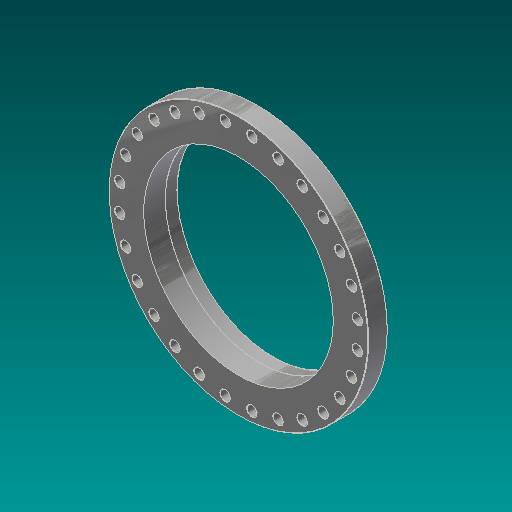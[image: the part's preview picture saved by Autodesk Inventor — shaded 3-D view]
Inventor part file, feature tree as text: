
AUTODESK INVENTOR PART (.ipt)
format: ipt  version: 2017.3 (Build 213257000, 257)  size: 361,472 bytes
history: native  units: in
note: dims shown in document units (in); Inventor stores cm internally (conversion verified against a paired STEP export)
features: sketch x7, extrude x5, chamfer x3, fillet x2, hole x1, pattern_circular x1, revolve x1, projected_geometry x1
ambient origin geometry x8: Origin, YZ Plane, XZ Plane, XY Plane, X Axis, Y Axis, Z Axis, Center Point
bodies: Solid1 (feature_tree)
feature tree (21):
  extrude  "Extrusion1"  Depth=31.0in
  extrude  "Extrusion2"  Depth=3.125in
  extrude  "Extrusion3"  Depth=32.75in
  hole  "Hole1"  [1 undecoded]
  chamfer  "Chamfer3"  Distance=11.0236in Angle=360.0deg
  pattern_circular  "Circular Pattern1"  [2 undecoded]
  chamfer  "Chamfer2"  Distance=0.0312in Angle=45.0deg
  fillet  "Fillet2"  Radius=0.1374in
  revolve  "Revolution3"  [1 undecoded]
  extrude  "Extrusion6"  Depth=0.5in
  extrude  "Extrusion7"  TaperAngle=90.0deg  [1 undecoded]
  fillet  "Fillet5"  Radius=0.2577in
  chamfer  "Chamfer9"  Distance=0.4375in
  sketch  "Sketch1"  dims[d0=41.75in d1=31.0in]
  sketch  "Sketch2"  dims[d2=3.125in d3=0.0in d4=36.0in]
  sketch  "Sketch3"  dims[d5=0.0625in d6=0.0in d7=32.75in]
  sketch  "Sketch4"  dims[d8=2.5in d9=0.0in d13=19.25in]
  sketch  "Sketch9"  dims[d14=0.0442in]
  sketch  "Sketch13"  dims[d15=1.625in d16=0.75in d17=0.375in d18=0.25in d19=0.5635in d20=1.0in d21=0.8108in d22=11.0236in d23=360.0deg]
  projected_geometry  "Projected Loop1"
  sketch  "Sketch14"  dims[d25=0.0625in d26=0.125in d27=0.0687in d29=0.4375in d30=0.0312in d31=0.125in d32=45.0deg d77=0.1374in d78=16.0in d79=0.5in d81=90.0deg d84=0.2577in d85=0.4375in d99=0.625in d119=0.0625in d120=0.0in d121=30.5in d122=3.5in d123=0.0in d124=0.0312in d125=0.0312in d126=0.125in d127=45.0deg]
note: 5 required parameter values undecoded (feature->parameter linkage not recoverable at this tier; creation-order binding heuristic only, values carry confidence <= 0.55)